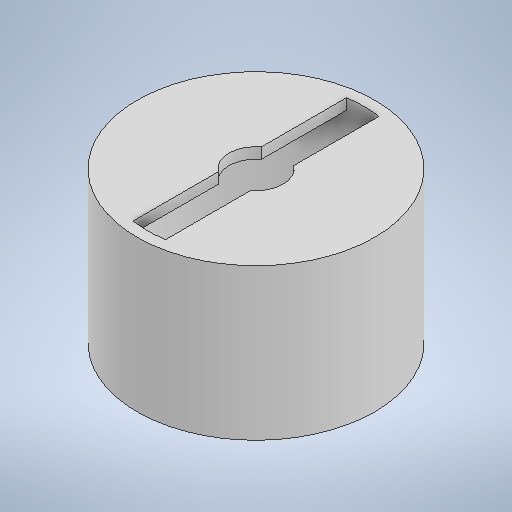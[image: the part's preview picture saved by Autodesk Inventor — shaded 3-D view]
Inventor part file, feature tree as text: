
AUTODESK INVENTOR PART (.ipt)
format: ipt  version: 2025.1 (Build 291241000, 241)  size: 222,208 bytes
history: native  units: mm
features: extrude x3, sketch x3
ambient origin geometry x8: Origin, YZ Plane, XZ Plane, XY Plane, X Axis, Y Axis, Z Axis, Center Point
bodies: Volumenkörper1 (feature_tree)
feature tree (6):
  extrude  "Extrusion1"  Depth=14.0mm TaperAngle=0.0deg
  extrude  "Extrusion2"  Depth=13.0mm TaperAngle=0.0deg
  extrude  "Extrusion3"  Depth=3.0mm
  sketch  "Skizze1"  dims[d0=22.0mm d1=14.0mm d2=0.0mm]
  sketch  "Skizze2"  dims[d3=1.0mm d4=13.0mm d5=0.0mm]
  sketch  "Skizze3"  dims[d6=5.0mm d7=3.0mm d8=1.5mm d9=11.0mm d10=0.0mm]
